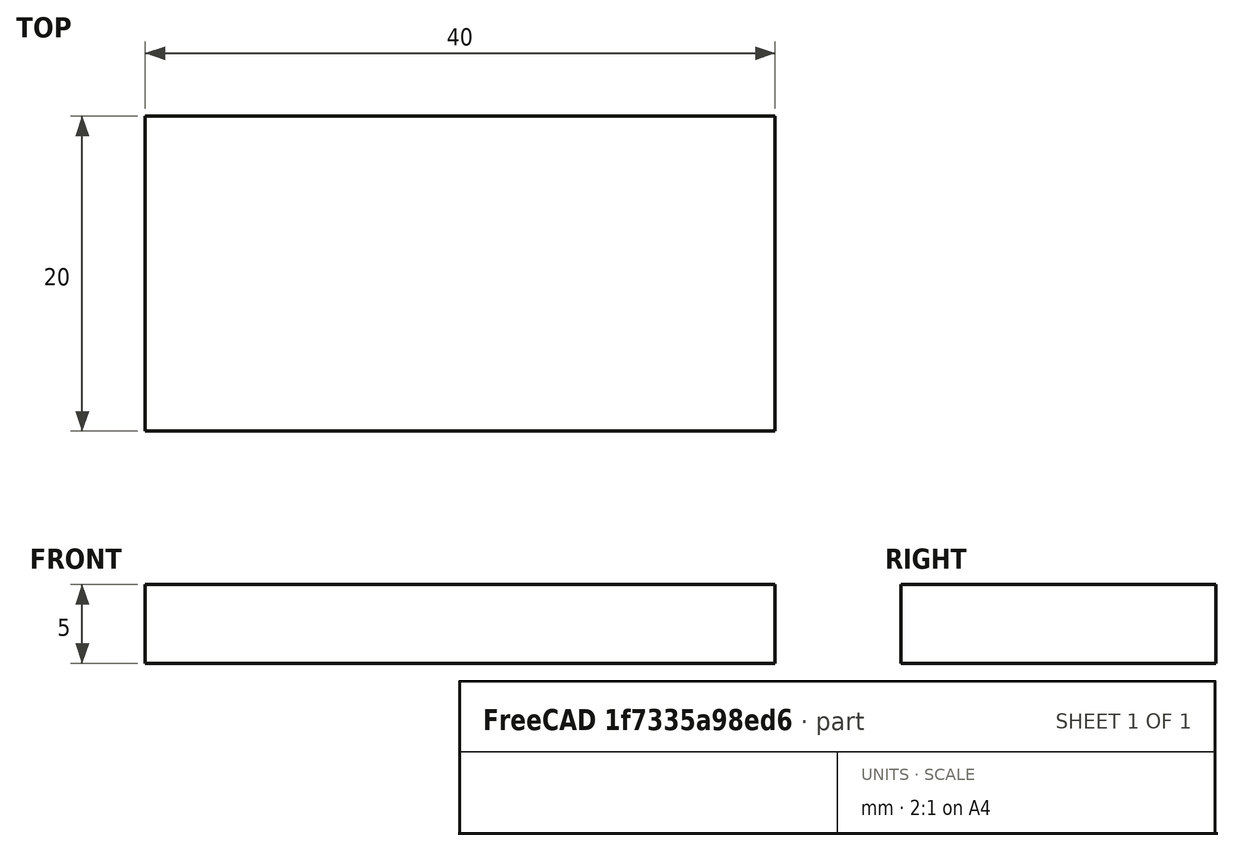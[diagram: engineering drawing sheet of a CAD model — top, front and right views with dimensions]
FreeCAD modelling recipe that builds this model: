
FCSTD DOCUMENT  (FreeCAD 0.20R29410 (Git))
Label: rectangulo_restringido
License: Creative Commons Attribution-ShareAlike
LicenseURL: http://creativecommons.org/licenses/by-sa/4.0/
objects: Sketcher::SketchObject×1, Part::Extrusion×1
note: 2 computed .brp shape members not serialized (recipe doc carries the construction recipe); baked Part::Feature solids carry a one-line shape summary decoded from their .brp

FEATURE [Sketcher::SketchObject] Sketch
  FullyConstrained = true
  sketch-geometry (4):
    g0: LineSegment StartX=0 StartY=20 StartZ=0 EndX=40 EndY=20 EndZ=0
    g1: LineSegment StartX=0 StartY=20 StartZ=0 EndX=0 EndY=0 EndZ=0
    g2: LineSegment StartX=0 StartY=0 StartZ=0 EndX=40 EndY=0 EndZ=0
    g3: LineSegment StartX=40 StartY=20 StartZ=0 EndX=40 EndY=0 EndZ=0
  constraints (11):
    c: Coincident(g0,g3)
    c: Coincident(g3,g2)
    c: Coincident(g1,g2)
    c: Coincident(g1,g0)
    c: Horizontal(g2)  'base'
    c: Horizontal(g0)  'base pero arriba'
    c: Vertical(g3)
    c: Vertical(g1)
    c: Coincident(g1,g-1)
    c: DistanceX(g0,g0) = 40  'lx'
    c: DistanceY(g2,g0) = 20  'h'
FEATURE [Part::Extrusion] Extrude
  Base = -> Sketch
  Dir = (0,0,1)
  DirMode = 2
  FaceMakerClass = Part::FaceMakerBullseye
  LengthFwd = 5
  LengthRev = 0
  Solid = true
  Symmetric = false
